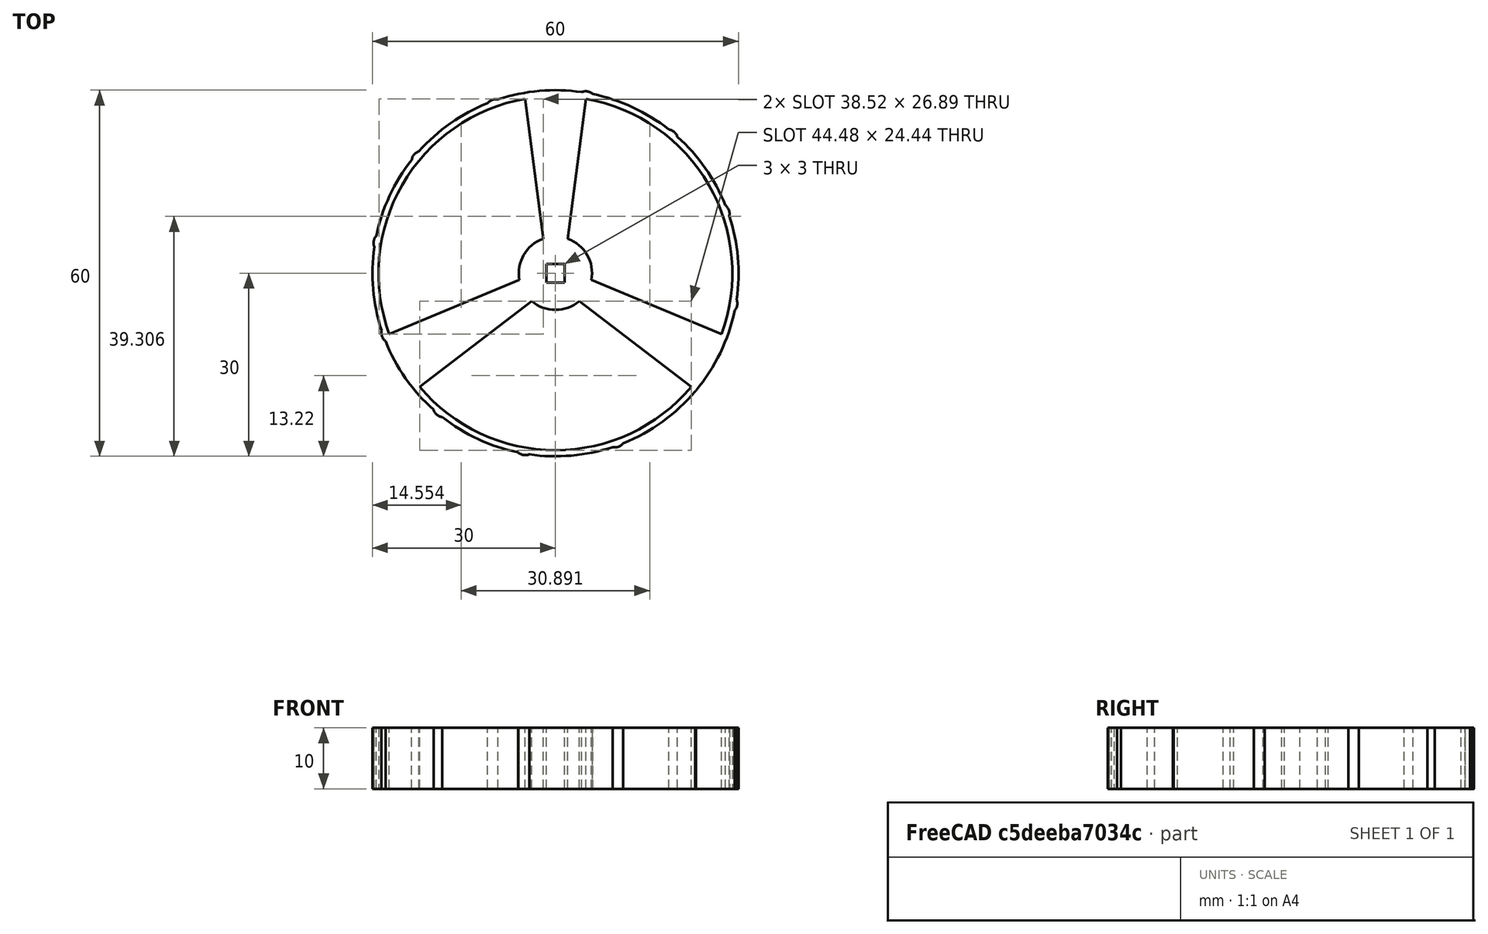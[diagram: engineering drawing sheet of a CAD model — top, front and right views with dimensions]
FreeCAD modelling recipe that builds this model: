
FCSTD DOCUMENT  (FreeCAD 0.20R29177 (Git))
Label: 3. neuer rad versuch
License: All rights reserved
LicenseURL: http://en.wikipedia.org/wiki/All_rights_reserved
objects: Sketcher::SketchObject×1, PartDesign::Pad×1, PartDesign::Body×1
note: 4 computed .brp shape members not serialized (recipe doc carries the construction recipe); baked Part::Feature solids carry a one-line shape summary decoded from their .brp

FEATURE [Sketcher::SketchObject] Sketch
  FullyConstrained = false
  MapMode = 5
  Support = -> [XY_Plane]
  sketch-geometry (56):
    g0: ArcOfCircle CenterX=0 CenterY=0 CenterZ=0 NormalX=0 NormalY=0 NormalZ=1 AngleXU=0 Radius=29 StartAngle=5.93287 EndAngle=7.6807
    g1: ArcOfCircle CenterX=0 CenterY=0 CenterZ=0 NormalX=0 NormalY=0 NormalZ=1 AngleXU=0 Radius=29 StartAngle=3.83847 EndAngle=5.58631
    g2: ArcOfCircle CenterX=0 CenterY=0 CenterZ=0 NormalX=0 NormalY=0 NormalZ=1 AngleXU=0 Radius=29 StartAngle=1.74408 EndAngle=3.49191
    g3: ArcOfCircle CenterX=0 CenterY=0 CenterZ=0 NormalX=0 NormalY=0 NormalZ=1 AngleXU=0 Radius=6 StartAngle=6.09942 EndAngle=7.51414
    g4: ArcOfCircle CenterX=0 CenterY=0 CenterZ=0 NormalX=0 NormalY=0 NormalZ=1 AngleXU=0 Radius=6 StartAngle=1.91063 EndAngle=3.32535
    g5: ArcOfCircle CenterX=0 CenterY=0 CenterZ=0 NormalX=0 NormalY=0 NormalZ=1 AngleXU=0 Radius=6 StartAngle=4.00503 EndAngle=5.41975
    g6: ArcOfCircle CenterX=0 CenterY=0 CenterZ=0 NormalX=0 NormalY=0 NormalZ=1 AngleXU=0 Radius=30 StartAngle=6.13948 EndAngle=6.60142
    g7: ArcOfCircle CenterX=0 CenterY=0 CenterZ=0 NormalX=0 NormalY=0 NormalZ=1 AngleXU=0 Radius=30 StartAngle=0.903493 EndAngle=1.36544
    g8: ArcOfCircle CenterX=0 CenterY=0 CenterZ=0 NormalX=0 NormalY=0 NormalZ=1 AngleXU=0 Radius=30 StartAngle=1.95069 EndAngle=2.41263
    g9: ArcOfCircle CenterX=0 CenterY=0 CenterZ=0 NormalX=0 NormalY=0 NormalZ=1 AngleXU=0 Radius=30 StartAngle=2.47429 EndAngle=2.93623
    g10: ArcOfCircle CenterX=0 CenterY=0 CenterZ=0 NormalX=0 NormalY=0 NormalZ=1 AngleXU=0 Radius=30 StartAngle=2.99789 EndAngle=3.45983
    g11: ArcOfCircle CenterX=0 CenterY=0 CenterZ=0 NormalX=0 NormalY=0 NormalZ=1 AngleXU=0 Radius=30 StartAngle=3.52149 EndAngle=3.98343
    g12: ArcOfCircle CenterX=0 CenterY=0 CenterZ=0 NormalX=0 NormalY=0 NormalZ=1 AngleXU=0 Radius=30 StartAngle=4.04509 EndAngle=4.50703
    g13: ArcOfCircle CenterX=0 CenterY=0 CenterZ=0 NormalX=0 NormalY=0 NormalZ=1 AngleXU=0 Radius=30 StartAngle=4.56868 EndAngle=5.03063
    g14: ArcOfCircle CenterX=0 CenterY=0 CenterZ=0 NormalX=0 NormalY=0 NormalZ=1 AngleXU=0 Radius=30 StartAngle=5.09228 EndAngle=5.58246
    g15: ArcOfCircle CenterX=0 CenterY=0 CenterZ=0 NormalX=0 NormalY=0 NormalZ=1 AngleXU=0 Radius=30 StartAngle=5.58765 EndAngle=6.07782
    g16: ArcOfCircle CenterX=21.642 CenterY=-18.1598 CenterZ=0 NormalX=0 NormalY=0 NormalZ=1 AngleXU=0 Radius=1.75 StartAngle=5.54061 EndAngle=5.6295
    g17: ArcOfCircle CenterX=28.067 CenterY=-4.94897 CenterZ=0 NormalX=0 NormalY=0 NormalZ=1 AngleXU=0 Radius=1.75 StartAngle=5.55194 EndAngle=6.66536
    g18: ArcOfCircle CenterX=26.7812 CenterY=9.74757 CenterZ=0 NormalX=0 NormalY=0 NormalZ=1 AngleXU=0 Radius=1.75 StartAngle=6.07554 EndAngle=7.18896
    g19: ArcOfCircle CenterX=18.3194 CenterY=21.8323 CenterZ=0 NormalX=0 NormalY=0 NormalZ=1 AngleXU=0 Radius=1.75 StartAngle=0.315953 EndAngle=1.42938
    g20: ArcOfCircle CenterX=-9.74757 CenterY=26.7812 CenterZ=0 NormalX=0 NormalY=0 NormalZ=1 AngleXU=0 Radius=1.75 StartAngle=1.36315 EndAngle=2.47657
    g21: ArcOfCircle CenterX=-21.8323 CenterY=18.3194 CenterZ=0 NormalX=0 NormalY=0 NormalZ=1 AngleXU=0 Radius=1.75 StartAngle=1.88675 EndAngle=3.00017
    g22: ArcOfCircle CenterX=-28.067 CenterY=4.94897 CenterZ=0 NormalX=0 NormalY=0 NormalZ=1 AngleXU=0 Radius=1.75 StartAngle=2.41035 EndAngle=3.52377
    g23: ArcOfCircle CenterX=-18.3194 CenterY=-21.8323 CenterZ=0 NormalX=0 NormalY=0 NormalZ=1 AngleXU=0 Radius=1.75 StartAngle=3.45755 EndAngle=4.57097
    g24: ArcOfCircle CenterX=-4.94897 CenterY=-28.067 CenterZ=0 NormalX=0 NormalY=0 NormalZ=1 AngleXU=0 Radius=1.75 StartAngle=3.98114 EndAngle=5.09457
    g25: ArcOfCircle CenterX=9.74757 CenterY=-26.7812 CenterZ=0 NormalX=0 NormalY=0 NormalZ=1 AngleXU=0 Radius=1.75 StartAngle=4.50474 EndAngle=5.61817
    g26: Circle CenterX=0 CenterY=0 CenterZ=0 NormalX=0 NormalY=0 NormalZ=1 AngleXU=0 Radius=28.5
    g27: LineSegment StartX=-1.5 StartY=1.5 StartZ=0 EndX=1.5 EndY=1.5 EndZ=0
    g28: LineSegment StartX=1.5 StartY=1.5 StartZ=0 EndX=1.5 EndY=-1.5 EndZ=0
    g29: LineSegment StartX=1.5 StartY=-1.5 StartZ=0 EndX=-1.5 EndY=-1.5 EndZ=0
    g30: LineSegment StartX=-1.5 StartY=-1.5 StartZ=0 EndX=-1.5 EndY=1.5 EndZ=0
    g31: LineSegment StartX=-3.89898 StartY=-4.56048 StartZ=0 EndX=-22.2386 EndY=-18.613 EndZ=0
    g32: LineSegment StartX=-5.89898 StartY=-1.09638 StartZ=0 EndX=-27.2386 EndY=-9.95273 EndZ=0
    g33: LineSegment StartX=-5 StartY=28.5657 StartZ=0 EndX=-2 EndY=5.65685 EndZ=0
    g34: LineSegment StartX=5 StartY=28.5657 StartZ=0 EndX=2 EndY=5.65685 EndZ=0
    g35: LineSegment StartX=5.89898 StartY=-1.09638 StartZ=0 EndX=27.2386 EndY=-9.95273 EndZ=0
    g36: LineSegment StartX=3.89898 StartY=-4.56048 StartZ=0 EndX=22.2386 EndY=-18.613 EndZ=0
    g37: LineSegment StartX=0 StartY=0 StartZ=0 EndX=24.6817 EndY=-14.25 EndZ=0
    g38: LineSegment StartX=0 StartY=0 StartZ=0 EndX=-24.6817 EndY=-14.25 EndZ=0
    g39: LineSegment StartX=-5.89898 StartY=-1.09638 StartZ=0 EndX=-3.89898 EndY=-4.56048 EndZ=0
    g40: LineSegment StartX=3.89898 StartY=-4.56048 StartZ=0 EndX=5.89898 EndY=-1.09638 EndZ=0
    g41: LineSegment StartX=-2 StartY=5.65685 StartZ=0 EndX=2 EndY=5.65685 EndZ=0
    g42: LineSegment StartX=27.2386 StartY=-9.95273 StartZ=0 EndX=22.2386 EndY=-18.613 EndZ=0
    g43: LineSegment StartX=-22.2386 StartY=-18.613 StartZ=0 EndX=-27.2386 EndY=-9.95273 EndZ=0
    g44: LineSegment StartX=-5 StartY=28.5657 StartZ=0 EndX=5 EndY=28.5657 EndZ=0
    g45: ArcOfCircle CenterX=0 CenterY=0 CenterZ=0 NormalX=0 NormalY=0 NormalZ=1 AngleXU=0 Radius=30 StartAngle=0.379894 EndAngle=0.841837
    g46: ArcOfCircle CenterX=4.94897 CenterY=28.067 CenterZ=0 NormalX=0 NormalY=0 NormalZ=1 AngleXU=0 Radius=1.75 StartAngle=0.839552 EndAngle=1.95297
    g47: ArcOfCircle CenterX=-26.7812 CenterY=-9.74757 CenterZ=0 NormalX=0 NormalY=0 NormalZ=1 AngleXU=0 Radius=1.75 StartAngle=2.93395 EndAngle=4.04737
    g48: ArcOfCircle CenterX=0 CenterY=0 CenterZ=0 NormalX=0 NormalY=0 NormalZ=1 AngleXU=0 Radius=30 StartAngle=1.42709 EndAngle=1.88903
    g49: LineSegment StartX=-9.74757 StartY=26.7812 StartZ=0 EndX=9.74757 EndY=-26.7812 EndZ=0
    g50: LineSegment StartX=4.94897 StartY=28.067 StartZ=0 EndX=-4.94897 EndY=-28.067 EndZ=0
    g51: LineSegment StartX=18.3194 StartY=21.8323 StartZ=0 EndX=-18.3194 EndY=-21.8323 EndZ=0
    g52: LineSegment StartX=21.642 StartY=-18.1598 StartZ=0 EndX=-21.8323 EndY=18.3194 EndZ=0
    g53: LineSegment StartX=26.7812 StartY=9.74757 StartZ=0 EndX=-26.7812 EndY=-9.74757 EndZ=0
    g54: LineSegment StartX=-28.067 StartY=4.94897 StartZ=0 EndX=28.067 EndY=-4.94897 EndZ=0
    g55: Circle CenterX=0 CenterY=0 CenterZ=0 NormalX=0 NormalY=0 NormalZ=1 AngleXU=0 Radius=30
  constraints (160):
    c: Coincident(g1,g0)
    c: Coincident(g2,g0)
    c: Horizontal(g2,g0)
    c: Equal(g2,g1)
    c: Coincident(g3,g0)
    c: Coincident(g4,g0)
    c: Coincident(g5,g0)
    c: Coincident(g7,g0)
    c: Coincident(g8,g0)
    c: Coincident(g9,g0)
    c: Coincident(g10,g0)
    c: Coincident(g11,g0)
    c: Coincident(g12,g0)
    c: Coincident(g13,g0)
    c: Coincident(g14,g0)
    c: Coincident(g15,g0)
    c: Coincident(g16,g15)
    c: Coincident(g16,g14)
    c: Coincident(g17,g6)
    c: Coincident(g17,g15)
    c: Coincident(g18,g6)
    c: Coincident(g19,g7)
    c: Coincident(g20,g8)
    c: Coincident(g21,g8)
    c: Coincident(g21,g9)
    c: Coincident(g22,g9)
    c: Coincident(g22,g10)
    c: Coincident(g23,g11)
    c: Coincident(g23,g12)
    c: Coincident(g24,g12)
    c: Coincident(g24,g13)
    c: Coincident(g25,g13)
    c: Coincident(g25,g14)
    c: Coincident(g26,g0)
    c: PointOnObject(g20,g26)
    c: PointOnObject(g21,g26)
    c: PointOnObject(g22,g26)
    c: PointOnObject(g23,g26)
    c: PointOnObject(g24,g26)
    c: PointOnObject(g25,g26)
    c: PointOnObject(g17,g26)
    c: Coincident(g0,g-1)
    c: Coincident(g27,g28)
    c: Coincident(g28,g29)
    c: Coincident(g29,g30)
    c: Coincident(g30,g27)
    c: Horizontal(g29)
    c: Vertical(g28)
    c: Symmetric(g27,g29,g-1)
    c: Symmetric(g27,g27,g-2)
    c: Equal(g27,g30)
    c: DistanceX(g27,g27) = 3
    c: Coincident(g31,g5)
    c: Coincident(g31,g1)
    c: Coincident(g32,g4)
    c: Coincident(g32,g2)
    c: Coincident(g33,g2)
    c: Coincident(g33,g4)
    c: Coincident(g34,g0)
    c: Coincident(g34,g3)
    c: Coincident(g35,g3)
    c: Coincident(g35,g0)
    c: Coincident(g36,g5)
    c: Coincident(g36,g1)
    c: Coincident(g37,g0)
    c: Coincident(g38,g0)
    c: Angle(g37,g-2) = 2.0944
    c: Angle(g-2,g38) = 2.0944
    c: PointOnObject(g38,g26)
    c: PointOnObject(g37,g26)
    c: Coincident(g39,g4)
    c: Coincident(g39,g5)
    c: Symmetric(g4,g5,g38)
    c: Coincident(g40,g5)
    c: Coincident(g40,g3)
    c: Symmetric(g3,g5,g37)
    c: Coincident(g41,g4)
    c: Coincident(g41,g3)
    c: Equal(g40,g41)
    c: Equal(g41,g39)
    c: Coincident(g42,g0)
    c: Coincident(g42,g1)
    c: Perpendicular(g37,g42)
    c: Coincident(g43,g1)
    c: Coincident(g43,g2)
    c: Perpendicular(g38,g43)
    c: Coincident(g44,g2)
    c: Coincident(g44,g0)
    c: Equal(g42,g44)
    c: Distance(g42) = 10
    c: Distance(g40) = 4
    c: Diameter(g3) = 12
    c: Coincident(g45,g18)
    c: Coincident(g45,g19)
    c: Coincident(g46,g7)
    c: Coincident(g45,g0)
    c: PointOnObject(g18,g26)
    c: PointOnObject(g19,g26)
    c: PointOnObject(g46,g26)
    c: PointOnObject(g47,g26)
    c: Coincident(g47,g11)
    c: Coincident(g47,g10)
    c: Equal(g47,g22)
    c: Equal(g22,g21)
    c: Equal(g21,g20)
    c: Equal(g20,g46)
    c: Equal(g46,g19)
    c: Equal(g19,g18)
    c: Equal(g18,g17)
    c: Equal(g17,g16)
    c: Equal(g16,g25)
    c: Equal(g25,g24)
    c: Equal(g24,g23)
    c: Coincident(g6,g0)
    c: Coincident(g48,g0)
    c: Coincident(g48,g46)
    c: Coincident(g48,g20)
    c: Diameter(g0) = 58
    c: Diameter(g26) = 57
    c: Symmetric(g2,g0,g-2)
    c: Coincident(g49,g20)
    c: Coincident(g49,g25)
    c: Coincident(g50,g46)
    c: Coincident(g50,g24)
    c: Coincident(g51,g19)
    c: Coincident(g51,g23)
    c: Coincident(g52,g16)
    c: Coincident(g52,g21)
    c: Coincident(g53,g18)
    c: Coincident(g53,g47)
    c: Coincident(g54,g22)
    c: Coincident(g54,g17)
    c: PointOnObject(g0,g50)
    c: PointOnObject(g0,g54)
    c: PointOnObject(g0,g49)
    c: PointOnObject(g0,g51)
    c: PointOnObject(g0,g53)
    c: PointOnObject(g0,g52)
    c: Angle(g50,g49) = 0.523599
    c: Angle(g51,g50) = 0.523599
    c: Angle(g53,g51) = 0.523599
    c: Angle(g54,g53) = 0.523599
    c: Angle(g-1,g54) = 2.96706
    c: Angle(g54,g52) = 2.61799
    c: Coincident(g55,g0)
    c: PointOnObject(g19,g55)
    c: PointOnObject(g46,g55)
    c: PointOnObject(g7,g55)
    c: PointOnObject(g6,g55)
    c: Diameter(g55) = 60
    c: PointOnObject(g13,g55)
    c: PointOnObject(g12,g55)
    c: PointOnObject(g14,g55)
    c: PointOnObject(g15,g55)
    c: PointOnObject(g11,g55)
    c: PointOnObject(g10,g55)
    c: PointOnObject(g9,g55)
    c: PointOnObject(g8,g55)
    c: Perpendicular(g-2,g41)
    c: Diameter(g46) = 3.5
FEATURE [PartDesign::Pad] Pad
  Direction = (0,0,1)
  Length = 10
  Length2 = 10
  Profile = -> Sketch
  ReferenceAxis = -> Sketch [N_Axis]
  Type = 0
FEATURE [PartDesign::Body] Body
  Group = -> [Sketch,Pad]
  Origin = -> Origin
  Tip = -> Pad
